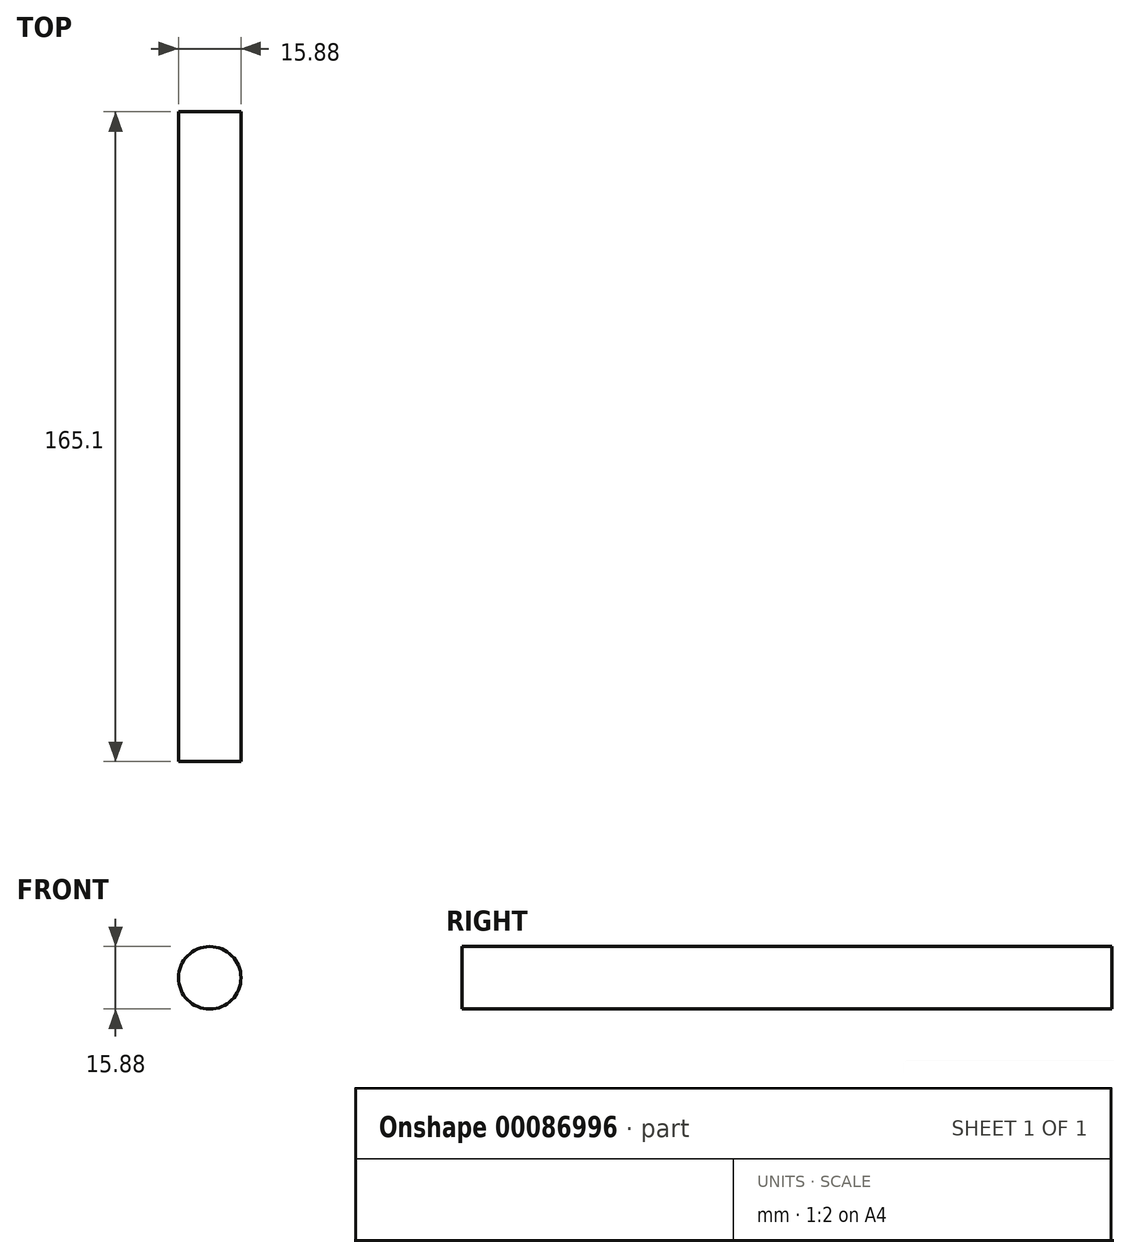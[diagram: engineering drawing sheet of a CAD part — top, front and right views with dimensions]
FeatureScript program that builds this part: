
annotation { "Feature Type Name" : "Feature", "Feature Type Description" : "" }
export const myFeature = defineFeature(function(context is Context, id is Id, definition is map)
    precondition{}
    {
        {
            var Q0;
            Q0=qCreatedBy(makeId("Front.planeOp"),FACE);
            var sketch = newSketch(context, id + "F0", { "sketchPlane" : qUnion([Q0])});
            skCircle(sketch, "E0", {"center": v(0, 0) * mm, "radius": 7.94 * mm});
            skSolve(sketch);
        }
        {
            var Q0;
            Q0=qSketchRegion(id+"F0",true);
            extrude(context, id + "F1", {"entities" : qUnion([Q0]), "depth" : 165.1 * mm});
        }
    });
